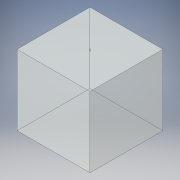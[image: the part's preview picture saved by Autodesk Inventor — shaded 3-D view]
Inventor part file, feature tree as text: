
AUTODESK INVENTOR PART (.ipt)
format: ipt  version: 2019.4 (Build 234330000, 330)  size: 99,328 bytes
history: native  units: mm
features: extrude x2, sketch x2
ambient origin geometry x8: Origin, YZ Plane, XZ Plane, XY Plane, X Axis, Y Axis, Z Axis, Center Point
bodies: Solid1 (feature_tree)
feature tree (4):
  extrude  "Extrusion1"  Depth=276.0mm
  extrude  "Extrusion2"  Depth=5.0mm
  sketch  "Sketch1"  dims[d0=276.0mm d1=276.0mm]
  sketch  "Sketch2"  dims[d2=267.0mm d3=0.0mm d4=4.0mm d5=138.0mm d6=5.0mm d7=0.0mm]
